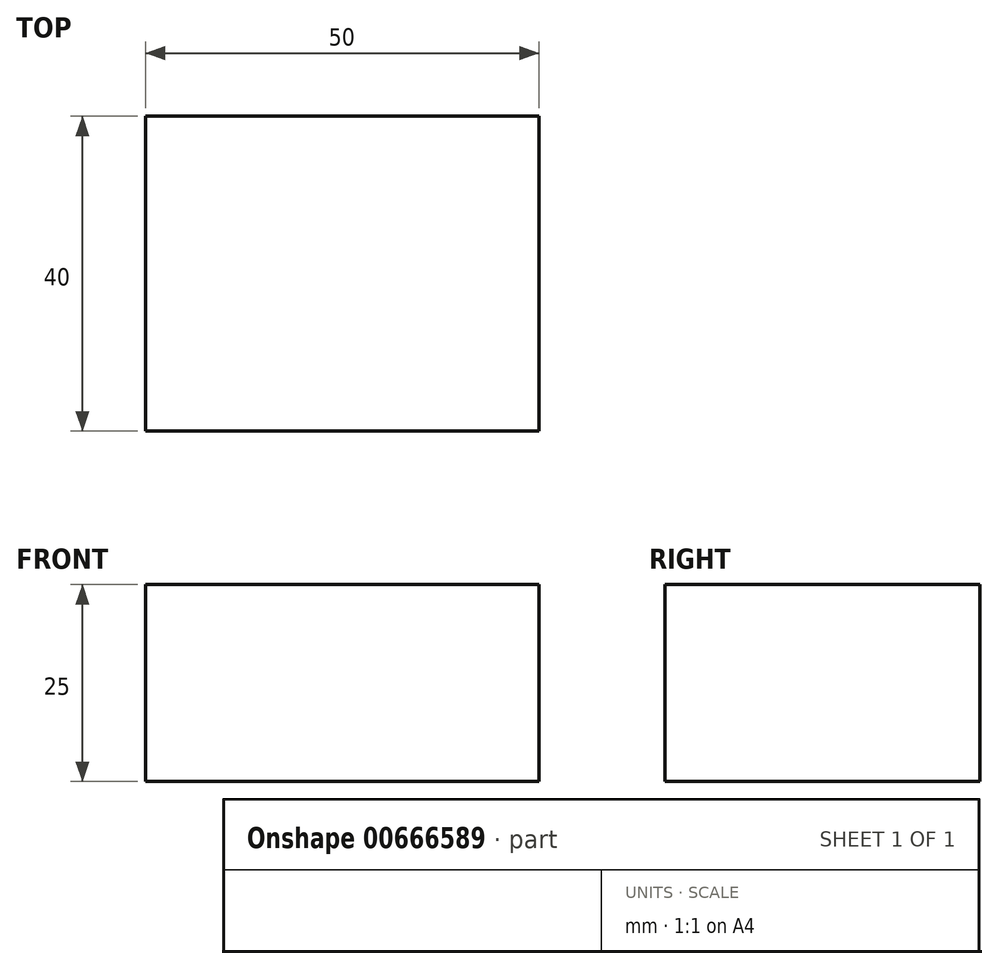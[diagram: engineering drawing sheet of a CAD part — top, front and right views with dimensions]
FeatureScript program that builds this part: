
annotation { "Feature Type Name" : "Feature", "Feature Type Description" : "" }
export const myFeature = defineFeature(function(context is Context, id is Id, definition is map)
    precondition{}
    {
        {
            var Q0;
            Q0=qCreatedBy(makeId("Top.planeOp"),FACE);
            var sketch = newSketch(context, id + "F0", { "sketchPlane" : qUnion([Q0])});
            skLineSegment(sketch, "E0.bottom", {"start": v(-74.4, 71.36) * mm, "end": v(75.6, 71.36) * mm});
            skLineSegment(sketch, "E0.top", {"start": v(-74.4, -8.64) * mm, "end": v(75.6, -8.64) * mm});
            skLineSegment(sketch, "E0.left", {"start": v(-74.4, 71.36) * mm, "end": v(-74.4, -8.64) * mm});
            skLineSegment(sketch, "E0.right", {"start": v(75.6, 71.36) * mm, "end": v(75.6, -8.64) * mm});
            skLineSegment(sketch, "E1.bottom", {"start": v(-74.4, 71.36) * mm, "end": v(-24.4, 71.36) * mm});
            skLineSegment(sketch, "E1.top", {"start": v(-74.4, 31.36) * mm, "end": v(-24.4, 31.36) * mm});
            skLineSegment(sketch, "E1.left", {"start": v(-74.4, 71.36) * mm, "end": v(-74.4, 31.36) * mm});
            skLineSegment(sketch, "E1.right", {"start": v(-24.4, 71.36) * mm, "end": v(-24.4, 31.36) * mm});
            skSolve(sketch);
        }
        {
            var Q0;
            Q0=makeQuery(id+"F0.imprint","IMPRINT",FACE,{"disambiguationData":[TD([[makeQuery(id+"F0.imprint","IMPRINT",EDGE,{"derivedFrom":sQuery(id+"F0.wireOp",EDGE,"E0.bottom")}),-1.0]])]});
            extrude(context, id + "F1", {"entities" : qUnion([Q0]), "depth" : 25 * mm, "offsetDistance" : 25 * mm});
        }
    });
